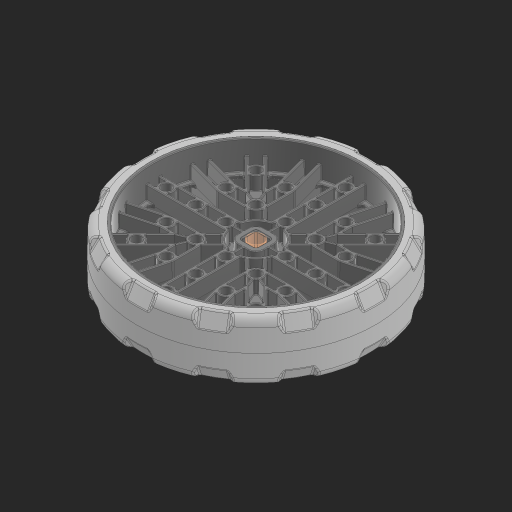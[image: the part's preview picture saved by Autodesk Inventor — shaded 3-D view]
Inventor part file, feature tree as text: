
AUTODESK INVENTOR PART (.ipt)
format: ipt  version: 2023 (Build 270158000, 158)  size: 10,181,632 bytes
history: native  units: in
note: dims shown in document units (in); Inventor stores cm internally (conversion verified against a paired STEP export)
features: other x3, sketch x1, extrude x1
ambient origin geometry x8: Origin, YZ Plane, XZ Plane, XY Plane, X Axis, Y Axis, Z Axis, Center Point
bodies: Solid1 (feature_tree), Solid2 (feature_tree)
feature tree (5):
  sketch  "Sketch1"  dims[d0=0.3937in d1=0.0in]
  other  "Srf1"
  other  "276-8103-001 Rev2_1:1"
  other  "276-8103-002 Rev2_2:1"
  extrude  "ExtrusionSrf1"  [1 undecoded]
note: 1 required parameter value undecoded (feature->parameter linkage not recoverable at this tier; creation-order binding heuristic only, values carry confidence <= 0.55)
